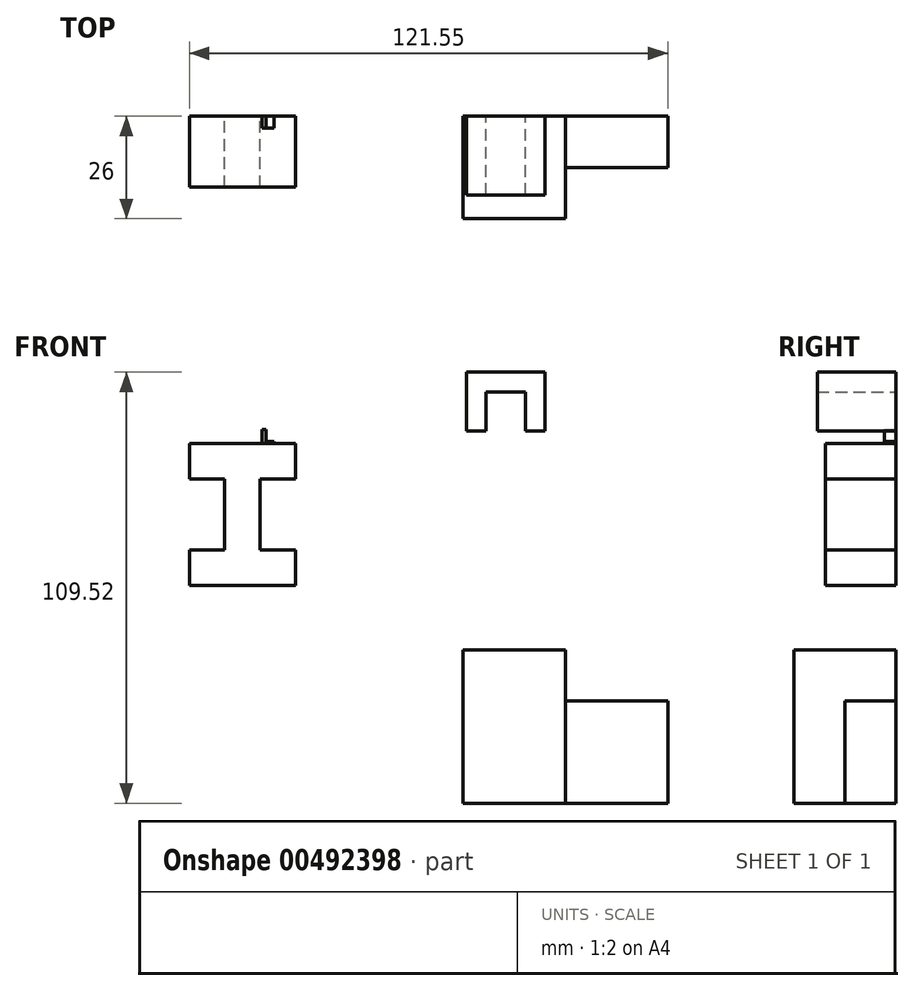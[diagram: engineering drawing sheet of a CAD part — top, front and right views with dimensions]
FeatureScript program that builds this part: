
annotation { "Feature Type Name" : "Feature", "Feature Type Description" : "" }
export const myFeature = defineFeature(function(context is Context, id is Id, definition is map)
    precondition{}
    {
        {
            var Q0;
            Q0=qCreatedBy(makeId("Front.planeOp"),FACE);
            var sketch = newSketch(context, id + "F0", { "sketchPlane" : qUnion([Q0])});
            skLineSegment(sketch, "E0", {"start": v(-33.07, 46.83) * mm, "end": v(-33.07, 42.83) * mm});
            skLineSegment(sketch, "E1", {"start": v(-33.07, 42.83) * mm, "end": v(-30.07, 42.83) * mm});
            skLineSegment(sketch, "E2", {"start": v(-30.07, 42.83) * mm, "end": v(-30.07, 43.83) * mm});
            skLineSegment(sketch, "E3", {"start": v(-30.07, 43.83) * mm, "end": v(-32.07, 43.83) * mm});
            skLineSegment(sketch, "E4", {"start": v(-32.07, 43.83) * mm, "end": v(-32.07, 46.83) * mm});
            skLineSegment(sketch, "E5", {"start": v(-32.07, 46.83) * mm, "end": v(-33.07, 46.83) * mm});
            skSolve(sketch);
        }
        {
            var Q0;
            Q0 = qSketchRegion(id + "F0", true);
            extrude(context, id + "F1", {"entities" : qUnion([Q0]), "depth" : 3 * mm});
        }
        {
            var Q0;
            Q0=qCreatedBy(makeId("Front.planeOp"),FACE);
            var sketch = newSketch(context, id + "F2", { "sketchPlane" : qUnion([Q0])});
            skLineSegment(sketch, "E6", {"start": v(18.86, 46.4) * mm, "end": v(18.86, 61.4) * mm});
            skLineSegment(sketch, "E7", {"start": v(18.86, 61.4) * mm, "end": v(38.86, 61.4) * mm});
            skLineSegment(sketch, "E8", {"start": v(38.86, 61.4) * mm, "end": v(38.86, 46.4) * mm});
            skLineSegment(sketch, "E9", {"start": v(38.86, 46.4) * mm, "end": v(33.86, 46.4) * mm});
            skLineSegment(sketch, "E10", {"start": v(33.86, 46.4) * mm, "end": v(33.86, 56.4) * mm});
            skLineSegment(sketch, "E11", {"start": v(33.86, 56.4) * mm, "end": v(23.86, 56.4) * mm});
            skLineSegment(sketch, "E12", {"start": v(23.86, 56.4) * mm, "end": v(23.86, 46.4) * mm});
            skLineSegment(sketch, "E13", {"start": v(23.86, 46.4) * mm, "end": v(18.86, 46.4) * mm});
            skSolve(sketch);
        }
        {
            var Q0;
            Q0 = qSketchRegion(id + "F2", true);
            extrude(context, id + "F3", {"entities" : qUnion([Q0]), "depth" : 20 * mm});
        }
        {
            var Q0;
            Q0=qCreatedBy(makeId("Front.planeOp"),FACE);
            var sketch = newSketch(context, id + "F4", { "sketchPlane" : qUnion([Q0])});
            skLineSegment(sketch, "E14.bottom", {"start": v(-51.54, 43.22) * mm, "end": v(-24.54, 43.22) * mm});
            skLineSegment(sketch, "E14.top", {"start": v(-51.54, 34.22) * mm, "end": v(-42.54, 34.22) * mm});
            skLineSegment(sketch, "E14.left", {"start": v(-51.54, 43.22) * mm, "end": v(-51.54, 34.22) * mm});
            skLineSegment(sketch, "E14.right", {"start": v(-24.54, 43.22) * mm, "end": v(-24.54, 34.22) * mm});
            skLineSegment(sketch, "E15.bottom", {"start": v(-51.54, 7.22) * mm, "end": v(-24.54, 7.22) * mm});
            skLineSegment(sketch, "E15.top", {"start": v(-51.54, 16.22) * mm, "end": v(-42.54, 16.22) * mm});
            skLineSegment(sketch, "E15.left", {"start": v(-51.54, 7.22) * mm, "end": v(-51.54, 16.22) * mm});
            skLineSegment(sketch, "E15.right", {"start": v(-24.54, 7.22) * mm, "end": v(-24.54, 16.22) * mm});
            skLineSegment(sketch, "E16.left", {"start": v(-42.54, 34.22) * mm, "end": v(-42.54, 16.22) * mm});
            skLineSegment(sketch, "E16.right", {"start": v(-33.54, 34.22) * mm, "end": v(-33.54, 16.22) * mm});
            skLineSegment(sketch, "E17.trimOffspring", {"start": v(-33.54, 34.22) * mm, "end": v(-24.54, 34.22) * mm});
            skLineSegment(sketch, "E18.trimOffspring", {"start": v(-33.54, 16.22) * mm, "end": v(-24.54, 16.22) * mm});
            skSolve(sketch);
        }
        {
            var Q0;
            Q0 = qSketchRegion(id + "F4", true);
            extrude(context, id + "F5", {"entities" : qUnion([Q0]), "operationType" : NewBodyOperationType.ADD, "depth" : 18 * mm});
        }
        {
            var Q0;
            Q0=qCreatedBy(makeId("Front.planeOp"),FACE);
            var sketch = newSketch(context, id + "F6", { "sketchPlane" : qUnion([Q0])});
            skLineSegment(sketch, "E19.bottom", {"start": v(18.01, -9.12) * mm, "end": v(44.01, -9.12) * mm});
            skLineSegment(sketch, "E19.top", {"start": v(18.01, -48.12) * mm, "end": v(44.01, -48.12) * mm});
            skLineSegment(sketch, "E19.left", {"start": v(18.01, -9.12) * mm, "end": v(18.01, -48.12) * mm});
            skLineSegment(sketch, "E19.right", {"start": v(44.01, -9.12) * mm, "end": v(44.01, -48.12) * mm});
            skSolve(sketch);
        }
        {
            var Q0;
            Q0 = qSketchRegion(id + "F6", true);
            extrude(context, id + "F7", {"entities" : qUnion([Q0]), "depth" : 26 * mm});
        }
        {
            var Q0;
            Q0=makeQuery(id+"F7.opExtrude","SWEPT_FACE",FACE,{"disambiguationData":[OSD([sQuery(id+"F6.wireOp",EDGE,"E19.right")])]});
            var sketch = newSketch(context, id + "F8", { "sketchPlane" : qUnion([Q0])});
            skLineSegment(sketch, "E20.bottom", {"start": v(-26, -9.12) * mm, "end": v(0, -9.12) * mm});
            skLineSegment(sketch, "E20.top", {"start": v(-26, -48.12) * mm, "end": v(0, -48.12) * mm});
            skLineSegment(sketch, "E20.left", {"start": v(-26, -9.12) * mm, "end": v(-26, -48.12) * mm});
            skLineSegment(sketch, "E20.right", {"start": v(0, -9.12) * mm, "end": v(0, -48.12) * mm});
            skLineSegment(sketch, "E21.bottom", {"start": v(-13, -22.12) * mm, "end": v(0, -22.12) * mm});
            skLineSegment(sketch, "E21.top", {"start": v(-13, -48.12) * mm, "end": v(0, -48.12) * mm});
            skLineSegment(sketch, "E21.left", {"start": v(-13, -22.12) * mm, "end": v(-13, -48.12) * mm});
            skLineSegment(sketch, "E21.right", {"start": v(0, -22.12) * mm, "end": v(0, -48.12) * mm});
            skSolve(sketch);
        }
        {
            var Q0;
            Q0=makeQuery(id+"F8.imprint","IMPRINT",FACE,{"disambiguationData":[TD([[makeQuery(id+"F8.imprint","IMPRINT",EDGE,{"derivedFrom":sQuery(id+"F8.wireOp",EDGE,"E21.bottom")}),-1.0]])]});
            extrude(context, id + "F9", {"entities" : qUnion([Q0]), "operationType" : NewBodyOperationType.ADD, "depth" : 26 * mm});
        }
    });
